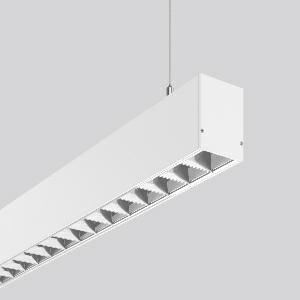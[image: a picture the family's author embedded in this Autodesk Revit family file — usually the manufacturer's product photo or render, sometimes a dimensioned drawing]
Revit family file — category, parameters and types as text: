
# Revit family: less_is_more_50_312335_002_2f92
name_source: partatom
category: Lighting Fixtures
units: mm (PartAtom-declared; Revit-internal decimal feet)

## family parameters
Cut with Voids When Loaded = No
Host = Face
Light Source = No
Part Type = Normal
Room Calculation Point = No
Round Connector Dimension = Use Diameter
Shared = No

## types (1)
- LESS IS MORE 50 (1 x LED Modul 830, 2500 lm, 3000)
    Apparent Load = 22 VA
    CIE Flux Codes = 95 100 100 100 100
    Color Rendering = 80
    Color Temperature = 3000
    Default Elevation = 1800 mm
    Description = Series: LESS IS MORE 50
Linear pendant luminaire for aesthetically sophisticated lighting. Housing: extruded aluminium profile, powder-coated. End cap aluminium powder-coated. Canopy made of aluminium, powder-coated. Alea optical system: Reflector structure (ABS, Aluminium-coated, highly polished) with integrated diffuser made of non-yellowing plastic (PMMA) opal for glare-free light at the workstation (screen-compliant according to EN 12464-1). Direct light emission. Suitable for pendant. 2-point steel cable suspension freely positionable and infinitely height-adjustable. Special lengths available on request. LED unit with integrated converter interchangeable and removable. Suitable for through-wiring. With sensors or as a safety luminaire on request. 
Colour: traffic white, matt (RAL 9016)
Length: 847 mm
Width: 57 mm
Height: 75 mm
Suspension length: 2000 mm
Lamp: LED
Socket: without socket
Colour temperature: 3000K
Colour rendering index (CRI): 80
System power: 22 W
Rated luminous flux: 2500 lm
Luminous efficiency: 114 lm/W
Control gear: Regulated power supply
Protection class: I
Type of protection: IP 20
    Height = 75 mm
    Lamp = 1 x LED Modul 830
    Lamp Light Flux = 2500 lm
    Lamp count = 1
    Length = 847 mm
    Lifetime = 50000 h
    Luminous efficacy = 114 lm/W
    Manufacturer = RZB
    ModVariant = No
    Model = 312335.002
    Mounting Place = Ceiling
    Mounting Type = Pendant
    Number of Poles = 1
    OnlyDefault = Yes
    Power Factor = 1
    Product Name = LESS IS MORE 50
    Product group = Pendant LED linear luminaires
    ProductGroupID = 907
    Protection Class = Protection class I
    Protection Degree = IP 20
    RLX_Detail_Level = 1
    RLX_Emergency_Light_Flux = 0 lm
    RLX_Emergency_Type = 0
    RLX_Emergency_Type_DB = No
    RlxData = <blob elided: 33125 chars, md5=d0d57bee>
    Socket = socket
    Standby Power = 0 W
    System Light Flux = 2500 lm
    System Power = 22 W
    Type Comments = Product without accessories
    Type Image = 312342.002.jpg
    URL = http://relux.com
    VarID = ---
    Voltage = 230 V
    Voltage Range = 220-240 V
    Weight = 0.00 kg
    Width = 57 mm

## geometry (parser evidence)
native form markers: Blend x4, Sweep x10
no freeform markers — native parametric forms only
